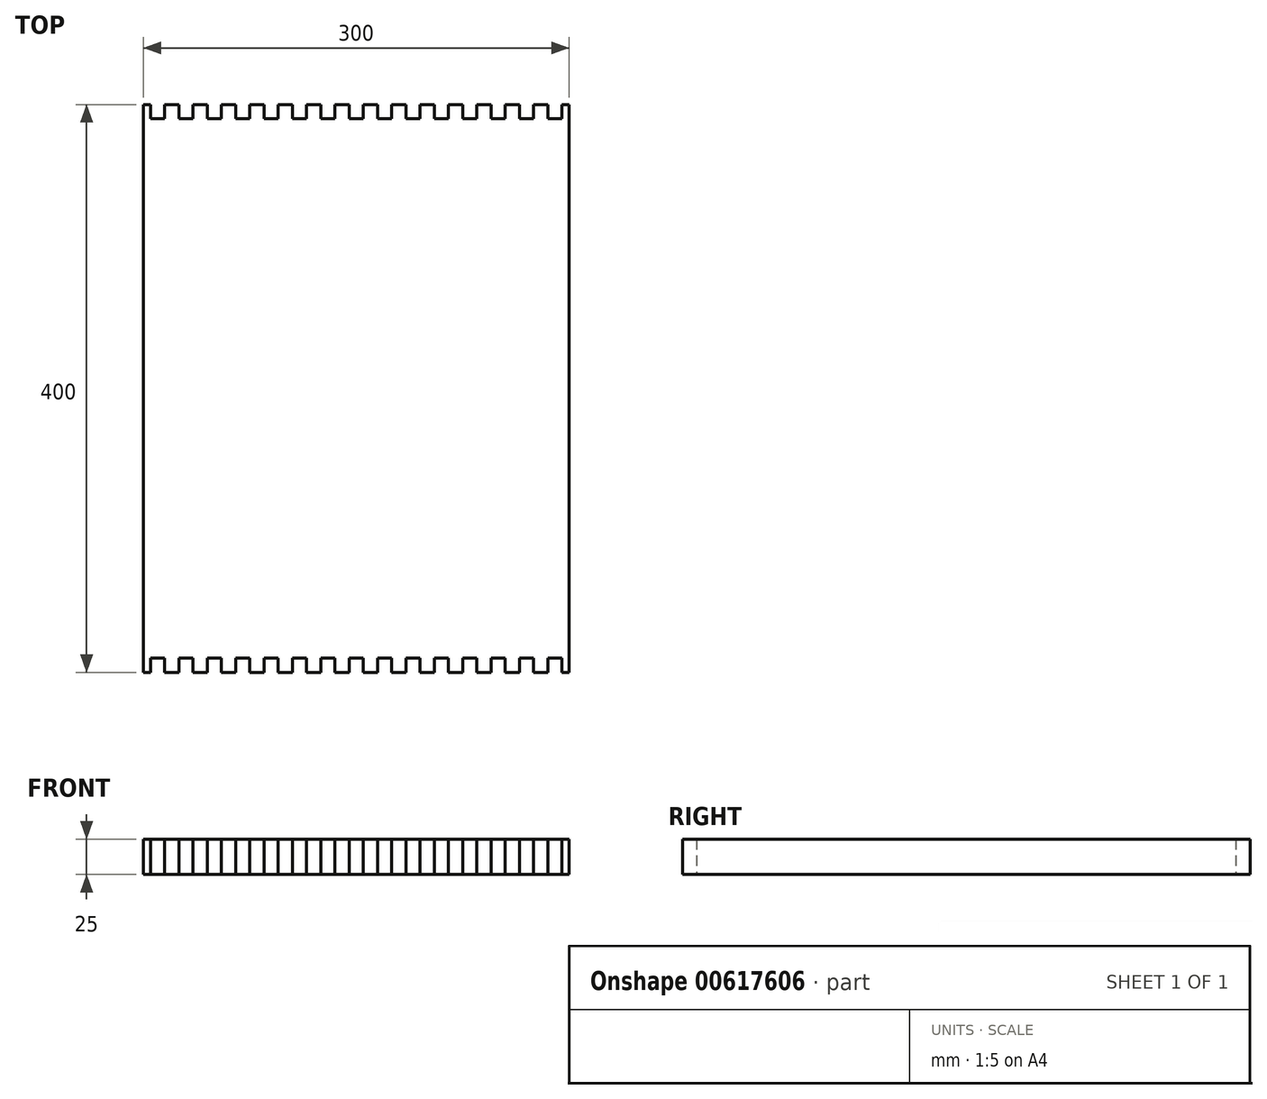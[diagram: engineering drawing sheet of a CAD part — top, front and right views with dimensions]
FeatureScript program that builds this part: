
annotation { "Feature Type Name" : "Feature", "Feature Type Description" : "" }
export const myFeature = defineFeature(function(context is Context, id is Id, definition is map)
    precondition{}
    {
        {
            var Q0;
            Q0=qCreatedBy(makeId("Top.planeOp"),FACE);
            var sketch = newSketch(context, id + "F0", { "sketchPlane" : qUnion([Q0])});
            skLineSegment(sketch, "E0.bottom", {"start": v(150, -200) * mm, "end": v(-150, -200) * mm});
            skLineSegment(sketch, "E0.top", {"start": v(150, 200) * mm, "end": v(-150, 200) * mm});
            skLineSegment(sketch, "E0.left", {"start": v(150, -200) * mm, "end": v(150, 200) * mm});
            skLineSegment(sketch, "E0.right", {"start": v(-150, -200) * mm, "end": v(-150, 200) * mm});
            skPoint(sketch, "E0.middle", {"position": v(0, 0) * mm});
            skLineSegment(sketch, "E1", {"start": v(0, -200) * mm, "end": v(-5, -200) * mm});
            skLineSegment(sketch, "E2.bottom", {"start": v(-5, -200) * mm, "end": v(5, -200) * mm});
            skLineSegment(sketch, "E2.top", {"start": v(-5, -190) * mm, "end": v(5, -190) * mm});
            skLineSegment(sketch, "E2.left", {"start": v(-5, -200) * mm, "end": v(-5, -190) * mm});
            skLineSegment(sketch, "E2.right", {"start": v(5, -200) * mm, "end": v(5, -190) * mm});
            skLineSegment(sketch, "E3.1.0.0", {"start": v(15, -190) * mm, "end": v(25, -190) * mm});
            skLineSegment(sketch, "E3.1.0.1", {"start": v(15, -200) * mm, "end": v(15, -190) * mm});
            skLineSegment(sketch, "E3.1.0.2", {"start": v(15, -200) * mm, "end": v(25, -200) * mm});
            skLineSegment(sketch, "E3.1.0.3", {"start": v(25, -200) * mm, "end": v(25, -190) * mm});
            skLineSegment(sketch, "E3.2.0.0", {"start": v(35, -190) * mm, "end": v(45, -190) * mm});
            skLineSegment(sketch, "E3.2.0.1", {"start": v(35, -200) * mm, "end": v(35, -190) * mm});
            skLineSegment(sketch, "E3.2.0.2", {"start": v(35, -200) * mm, "end": v(45, -200) * mm});
            skLineSegment(sketch, "E3.2.0.3", {"start": v(45, -200) * mm, "end": v(45, -190) * mm});
            skLineSegment(sketch, "E3.3.0.0", {"start": v(55, -190) * mm, "end": v(65, -190) * mm});
            skLineSegment(sketch, "E3.3.0.1", {"start": v(55, -200) * mm, "end": v(55, -190) * mm});
            skLineSegment(sketch, "E3.3.0.2", {"start": v(55, -200) * mm, "end": v(65, -200) * mm});
            skLineSegment(sketch, "E3.3.0.3", {"start": v(65, -200) * mm, "end": v(65, -190) * mm});
            skLineSegment(sketch, "E3.4.0.0", {"start": v(75, -190) * mm, "end": v(85, -190) * mm});
            skLineSegment(sketch, "E3.4.0.1", {"start": v(75, -200) * mm, "end": v(75, -190) * mm});
            skLineSegment(sketch, "E3.4.0.2", {"start": v(75, -200) * mm, "end": v(85, -200) * mm});
            skLineSegment(sketch, "E3.4.0.3", {"start": v(85, -200) * mm, "end": v(85, -190) * mm});
            skLineSegment(sketch, "E3.5.0.0", {"start": v(95, -190) * mm, "end": v(105, -190) * mm});
            skLineSegment(sketch, "E3.5.0.1", {"start": v(95, -200) * mm, "end": v(95, -190) * mm});
            skLineSegment(sketch, "E3.5.0.2", {"start": v(95, -200) * mm, "end": v(105, -200) * mm});
            skLineSegment(sketch, "E3.5.0.3", {"start": v(105, -200) * mm, "end": v(105, -190) * mm});
            skLineSegment(sketch, "E3.6.0.0", {"start": v(115, -190) * mm, "end": v(125, -190) * mm});
            skLineSegment(sketch, "E3.6.0.1", {"start": v(115, -200) * mm, "end": v(115, -190) * mm});
            skLineSegment(sketch, "E3.6.0.2", {"start": v(115, -200) * mm, "end": v(125, -200) * mm});
            skLineSegment(sketch, "E3.6.0.3", {"start": v(125, -200) * mm, "end": v(125, -190) * mm});
            skLineSegment(sketch, "E3.7.0.0", {"start": v(135, -190) * mm, "end": v(145, -190) * mm});
            skLineSegment(sketch, "E3.7.0.1", {"start": v(135, -200) * mm, "end": v(135, -190) * mm});
            skLineSegment(sketch, "E3.7.0.2", {"start": v(135, -200) * mm, "end": v(145, -200) * mm});
            skLineSegment(sketch, "E3.7.0.3", {"start": v(145, -200) * mm, "end": v(145, -190) * mm});
            skLineSegment(sketch, "E4.1.0.0", {"start": v(-25, -200) * mm, "end": v(-25, -190) * mm});
            skLineSegment(sketch, "E4.1.0.1", {"start": v(-25, -190) * mm, "end": v(-15, -190) * mm});
            skLineSegment(sketch, "E4.1.0.2", {"start": v(-15, -200) * mm, "end": v(-15, -190) * mm});
            skLineSegment(sketch, "E4.1.0.3", {"start": v(-25, -200) * mm, "end": v(-15, -200) * mm});
            skLineSegment(sketch, "E4.2.0.0", {"start": v(-45, -200) * mm, "end": v(-45, -190) * mm});
            skLineSegment(sketch, "E4.2.0.1", {"start": v(-45, -190) * mm, "end": v(-35, -190) * mm});
            skLineSegment(sketch, "E4.2.0.2", {"start": v(-35, -200) * mm, "end": v(-35, -190) * mm});
            skLineSegment(sketch, "E4.2.0.3", {"start": v(-45, -200) * mm, "end": v(-35, -200) * mm});
            skLineSegment(sketch, "E4.3.0.0", {"start": v(-65, -200) * mm, "end": v(-65, -190) * mm});
            skLineSegment(sketch, "E4.3.0.1", {"start": v(-65, -190) * mm, "end": v(-55, -190) * mm});
            skLineSegment(sketch, "E4.3.0.2", {"start": v(-55, -200) * mm, "end": v(-55, -190) * mm});
            skLineSegment(sketch, "E4.3.0.3", {"start": v(-65, -200) * mm, "end": v(-55, -200) * mm});
            skLineSegment(sketch, "E4.4.0.0", {"start": v(-85, -200) * mm, "end": v(-85, -190) * mm});
            skLineSegment(sketch, "E4.4.0.1", {"start": v(-85, -190) * mm, "end": v(-75, -190) * mm});
            skLineSegment(sketch, "E4.4.0.2", {"start": v(-75, -200) * mm, "end": v(-75, -190) * mm});
            skLineSegment(sketch, "E4.4.0.3", {"start": v(-85, -200) * mm, "end": v(-75, -200) * mm});
            skLineSegment(sketch, "E4.5.0.0", {"start": v(-105, -200) * mm, "end": v(-105, -190) * mm});
            skLineSegment(sketch, "E4.5.0.1", {"start": v(-105, -190) * mm, "end": v(-95, -190) * mm});
            skLineSegment(sketch, "E4.5.0.2", {"start": v(-95, -200) * mm, "end": v(-95, -190) * mm});
            skLineSegment(sketch, "E4.5.0.3", {"start": v(-105, -200) * mm, "end": v(-95, -200) * mm});
            skLineSegment(sketch, "E4.6.0.0", {"start": v(-125, -200) * mm, "end": v(-125, -190) * mm});
            skLineSegment(sketch, "E4.6.0.1", {"start": v(-125, -190) * mm, "end": v(-115, -190) * mm});
            skLineSegment(sketch, "E4.6.0.2", {"start": v(-115, -200) * mm, "end": v(-115, -190) * mm});
            skLineSegment(sketch, "E4.6.0.3", {"start": v(-125, -200) * mm, "end": v(-115, -200) * mm});
            skLineSegment(sketch, "E4.7.0.0", {"start": v(-145, -200) * mm, "end": v(-145, -190) * mm});
            skLineSegment(sketch, "E4.7.0.1", {"start": v(-145, -190) * mm, "end": v(-135, -190) * mm});
            skLineSegment(sketch, "E4.7.0.2", {"start": v(-135, -200) * mm, "end": v(-135, -190) * mm});
            skLineSegment(sketch, "E4.7.0.3", {"start": v(-145, -200) * mm, "end": v(-135, -200) * mm});
            skLineSegment(sketch, "E4.direction1", {"start": v(-5, -200) * mm, "end": v(-25, -200) * mm, "construction": true});
            skLineSegment(sketch, "E5.MirrorCS", {"start": v(-145, 190) * mm, "end": v(-135, 190) * mm});
            skLineSegment(sketch, "E6.MirrorCS", {"start": v(-145, 200) * mm, "end": v(-145, 190) * mm});
            skLineSegment(sketch, "E7.MirrorCS", {"start": v(-25, 200) * mm, "end": v(-25, 190) * mm});
            skLineSegment(sketch, "E8.MirrorCS", {"start": v(-25, 200) * mm, "end": v(-15, 200) * mm});
            skLineSegment(sketch, "E9.MirrorCS", {"start": v(85, 200) * mm, "end": v(85, 190) * mm});
            skLineSegment(sketch, "E10.MirrorCS", {"start": v(-35, 200) * mm, "end": v(-35, 190) * mm});
            skLineSegment(sketch, "E11.MirrorCS", {"start": v(-45, 200) * mm, "end": v(-45, 190) * mm});
            skLineSegment(sketch, "E12.MirrorCS", {"start": v(-65, 200) * mm, "end": v(-55, 200) * mm});
            skLineSegment(sketch, "E13.MirrorCS", {"start": v(75, 200) * mm, "end": v(85, 200) * mm});
            skLineSegment(sketch, "E14.MirrorCS", {"start": v(45, 200) * mm, "end": v(45, 190) * mm});
            skLineSegment(sketch, "E15.MirrorCS", {"start": v(-15, 200) * mm, "end": v(-15, 190) * mm});
            skLineSegment(sketch, "E16.MirrorCS", {"start": v(-55, 200) * mm, "end": v(-55, 190) * mm});
            skLineSegment(sketch, "E17.MirrorCS", {"start": v(75, 200) * mm, "end": v(75, 190) * mm});
            skLineSegment(sketch, "E18.MirrorCS", {"start": v(35, 200) * mm, "end": v(45, 200) * mm});
            skLineSegment(sketch, "E19.MirrorCS", {"start": v(-25, 190) * mm, "end": v(-15, 190) * mm});
            skLineSegment(sketch, "E20.MirrorCS", {"start": v(-65, 190) * mm, "end": v(-55, 190) * mm});
            skLineSegment(sketch, "E21.MirrorCS", {"start": v(35, 200) * mm, "end": v(35, 190) * mm});
            skLineSegment(sketch, "E22.MirrorCS", {"start": v(75, 190) * mm, "end": v(85, 190) * mm});
            skLineSegment(sketch, "E23.MirrorCS", {"start": v(15, 200) * mm, "end": v(15, 190) * mm});
            skLineSegment(sketch, "E24.MirrorCS", {"start": v(15, 190) * mm, "end": v(25, 190) * mm});
            skLineSegment(sketch, "E25.MirrorCS", {"start": v(5, 200) * mm, "end": v(5, 190) * mm});
            skLineSegment(sketch, "E26.MirrorCS", {"start": v(-5, 200) * mm, "end": v(-5, 190) * mm});
            skLineSegment(sketch, "E27.MirrorCS", {"start": v(-5, 190) * mm, "end": v(5, 190) * mm});
            skLineSegment(sketch, "E28.MirrorCS", {"start": v(-5, 200) * mm, "end": v(5, 200) * mm});
            skLineSegment(sketch, "E29.MirrorCS", {"start": v(0, 200) * mm, "end": v(-5, 200) * mm});
            skLineSegment(sketch, "E30.MirrorCS", {"start": v(-5, 200) * mm, "end": v(-25, 200) * mm, "construction": true});
            skLineSegment(sketch, "E31.MirrorCS", {"start": v(-85, 200) * mm, "end": v(-85, 190) * mm});
            skLineSegment(sketch, "E32.MirrorCS", {"start": v(-45, 200) * mm, "end": v(-35, 200) * mm});
            skLineSegment(sketch, "E33.MirrorCS", {"start": v(-75, 200) * mm, "end": v(-75, 190) * mm});
            skLineSegment(sketch, "E34.MirrorCS", {"start": v(55, 190) * mm, "end": v(65, 190) * mm});
            skLineSegment(sketch, "E35.MirrorCS", {"start": v(-65, 200) * mm, "end": v(-65, 190) * mm});
            skLineSegment(sketch, "E36.MirrorCS", {"start": v(65, 200) * mm, "end": v(65, 190) * mm});
            skLineSegment(sketch, "E37.MirrorCS", {"start": v(-85, 200) * mm, "end": v(-75, 200) * mm});
            skLineSegment(sketch, "E38.MirrorCS", {"start": v(15, 200) * mm, "end": v(25, 200) * mm});
            skLineSegment(sketch, "E39.MirrorCS", {"start": v(25, 200) * mm, "end": v(25, 190) * mm});
            skLineSegment(sketch, "E40.MirrorCS", {"start": v(35, 190) * mm, "end": v(45, 190) * mm});
            skLineSegment(sketch, "E41.MirrorCS", {"start": v(95, 200) * mm, "end": v(105, 200) * mm});
            skLineSegment(sketch, "E42.MirrorCS", {"start": v(-85, 190) * mm, "end": v(-75, 190) * mm});
            skLineSegment(sketch, "E43.MirrorCS", {"start": v(-115, 200) * mm, "end": v(-115, 190) * mm});
            skLineSegment(sketch, "E44.MirrorCS", {"start": v(-45, 190) * mm, "end": v(-35, 190) * mm});
            skLineSegment(sketch, "E45.MirrorCS", {"start": v(95, 200) * mm, "end": v(95, 190) * mm});
            skLineSegment(sketch, "E46.MirrorCS", {"start": v(55, 200) * mm, "end": v(65, 200) * mm});
            skLineSegment(sketch, "E47.MirrorCS", {"start": v(95, 190) * mm, "end": v(105, 190) * mm});
            skLineSegment(sketch, "E48.MirrorCS", {"start": v(55, 200) * mm, "end": v(55, 190) * mm});
            skLineSegment(sketch, "E49.MirrorCS", {"start": v(125, 200) * mm, "end": v(125, 190) * mm});
            skLineSegment(sketch, "E50.MirrorCS", {"start": v(-95, 200) * mm, "end": v(-95, 190) * mm});
            skLineSegment(sketch, "E51.MirrorCS", {"start": v(115, 200) * mm, "end": v(125, 200) * mm});
            skLineSegment(sketch, "E52.MirrorCS", {"start": v(-105, 190) * mm, "end": v(-95, 190) * mm});
            skLineSegment(sketch, "E53.MirrorCS", {"start": v(115, 200) * mm, "end": v(115, 190) * mm});
            skLineSegment(sketch, "E54.MirrorCS", {"start": v(-105, 200) * mm, "end": v(-105, 190) * mm});
            skLineSegment(sketch, "E55.MirrorCS", {"start": v(135, 190) * mm, "end": v(145, 190) * mm});
            skLineSegment(sketch, "E56.MirrorCS", {"start": v(105, 200) * mm, "end": v(105, 190) * mm});
            skLineSegment(sketch, "E57.MirrorCS", {"start": v(135, 200) * mm, "end": v(145, 200) * mm});
            skLineSegment(sketch, "E58.MirrorCS", {"start": v(-105, 200) * mm, "end": v(-95, 200) * mm});
            skLineSegment(sketch, "E59.MirrorCS", {"start": v(115, 190) * mm, "end": v(125, 190) * mm});
            skLineSegment(sketch, "E60.MirrorCS", {"start": v(-125, 190) * mm, "end": v(-115, 190) * mm});
            skLineSegment(sketch, "E61.MirrorCS", {"start": v(135, 200) * mm, "end": v(135, 190) * mm});
            skLineSegment(sketch, "E62.MirrorCS", {"start": v(-125, 200) * mm, "end": v(-125, 190) * mm});
            skLineSegment(sketch, "E63.MirrorCS", {"start": v(-125, 200) * mm, "end": v(-115, 200) * mm});
            skLineSegment(sketch, "E64.MirrorCS", {"start": v(145, 200) * mm, "end": v(145, 190) * mm});
            skLineSegment(sketch, "E65.MirrorCS", {"start": v(-145, 200) * mm, "end": v(-135, 200) * mm});
            skLineSegment(sketch, "E66.MirrorCS", {"start": v(-135, 200) * mm, "end": v(-135, 190) * mm});
            skSolve(sketch);
        }
        {
            var Q0;
            {var subQ28=sQuery(id+"F0.wireOp",EDGE,"E0.left");Q0=makeQuery(id+"F0.imprint","IMPRINT",FACE,{"disambiguationData":[TD([[makeQuery(id+"F0.imprint","IMPRINT",EDGE,{"derivedFrom":subQ28}),1.0]])]});}
            extrude(context, id + "F1", {"entities" : qUnion([Q0]), "depth" : 25 * mm, "offsetDistance" : 25 * mm});
        }
    });
